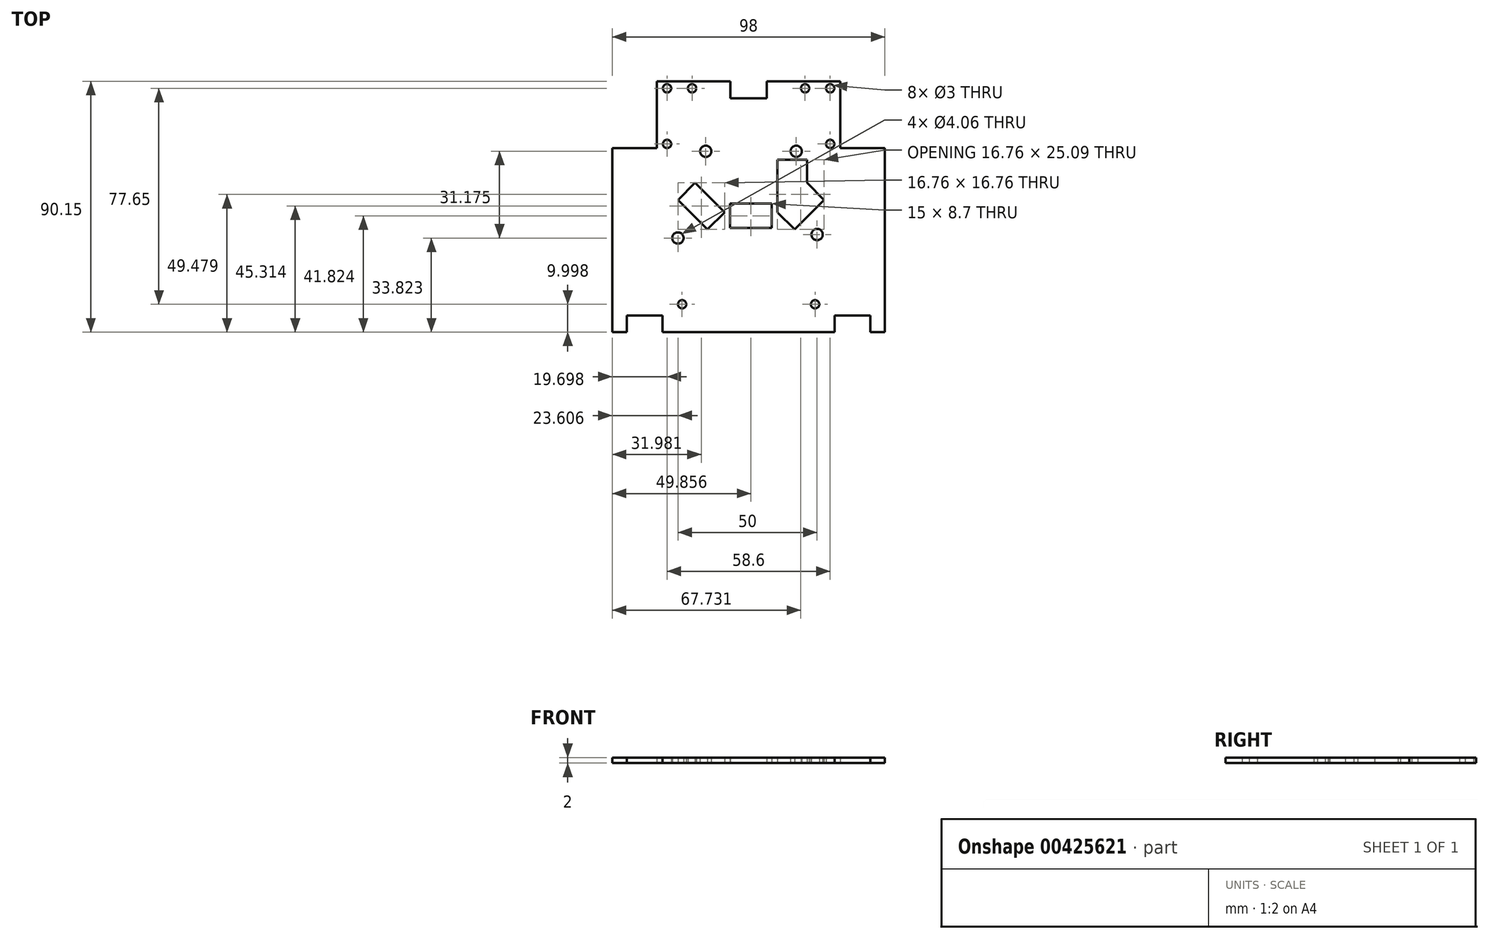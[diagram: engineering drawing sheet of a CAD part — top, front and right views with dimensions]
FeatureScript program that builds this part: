
annotation { "Feature Type Name" : "Feature", "Feature Type Description" : "" }
export const myFeature = defineFeature(function(context is Context, id is Id, definition is map)
    precondition{}
    {
        {
            var Q0;
            Q0=qCreatedBy(makeId("Top.planeOp"),FACE);
            var sketch = newSketch(context, id + "F0", { "sketchPlane" : qUnion([Q0])});
            skCircle(sketch, "E0", {"center": v(21.8, -32.76) * mm, "radius": 1.5 * mm});
            skCircle(sketch, "E1", {"center": v(18.2, 44.89) * mm, "radius": 1.5 * mm});
            skCircle(sketch, "E2", {"center": v(27.2, 24.89) * mm, "radius": 1.5 * mm});
            skCircle(sketch, "E3", {"center": v(-31.4, 44.89) * mm, "radius": 1.5 * mm});
            skCircle(sketch, "E4", {"center": v(27.2, 44.89) * mm, "radius": 1.5 * mm});
            skCircle(sketch, "E5", {"center": v(-22.4, 44.89) * mm, "radius": 1.5 * mm});
            skCircle(sketch, "E6", {"center": v(-31.4, 24.89) * mm, "radius": 1.5 * mm});
            skLineSegment(sketch, "E7", {"start": v(46.9, -42.76) * mm, "end": v(41.62, -42.76) * mm});
            skLineSegment(sketch, "E8", {"start": v(-51.1, -42.76) * mm, "end": v(-51.1, 23.39) * mm});
            skLineSegment(sketch, "E9", {"start": v(-35.1, 23.39) * mm, "end": v(-35.1, 47.39) * mm});
            skLineSegment(sketch, "E10", {"start": v(-35.1, 47.39) * mm, "end": v(-8.6, 47.39) * mm});
            skLineSegment(sketch, "E11", {"start": v(30.9, 47.39) * mm, "end": v(30.9, 23.39) * mm});
            skLineSegment(sketch, "E12", {"start": v(46.9, 23.39) * mm, "end": v(46.9, -42.76) * mm});
            skCircle(sketch, "E13", {"center": v(-27.5, -8.94) * mm, "radius": 2.03 * mm});
            skCircle(sketch, "E14", {"center": v(-17.5, 22.24) * mm, "radius": 2.03 * mm});
            skCircle(sketch, "E15", {"center": v(15, 22.24) * mm, "radius": 2.03 * mm});
            skCircle(sketch, "E16", {"center": v(22.5, -7.69) * mm, "radius": 2.03 * mm});
            skLineSegment(sketch, "E17", {"start": v(-8.74, 3.41) * mm, "end": v(6.26, 3.41) * mm});
            skLineSegment(sketch, "E18", {"start": v(-8.74, 3.41) * mm, "end": v(-8.74, -5.29) * mm});
            skLineSegment(sketch, "E19", {"start": v(-8.74, -5.29) * mm, "end": v(6.26, -5.29) * mm});
            skLineSegment(sketch, "E20", {"start": v(6.26, 3.41) * mm, "end": v(6.26, -5.29) * mm});
            skLineSegment(sketch, "E21", {"start": v(-10.74, 0.33) * mm, "end": v(-16.9, -5.83) * mm});
            skLineSegment(sketch, "E22", {"start": v(-10.74, 0.33) * mm, "end": v(-21.35, 10.93) * mm});
            skLineSegment(sketch, "E23", {"start": v(-21.35, 10.93) * mm, "end": v(-27.5, 4.78) * mm});
            skLineSegment(sketch, "E24", {"start": v(-16.9, -5.83) * mm, "end": v(-27.5, 4.78) * mm});
            skLineSegment(sketch, "E25", {"start": v(8.25, 0.33) * mm, "end": v(14.4, -5.83) * mm});
            skLineSegment(sketch, "E26", {"start": v(14.4, -5.83) * mm, "end": v(25.01, 4.78) * mm});
            skLineSegment(sketch, "E27", {"start": v(18.86, 10.93) * mm, "end": v(25.01, 4.78) * mm});
            skCircle(sketch, "E28", {"center": v(-26, -32.76) * mm, "radius": 1.5 * mm});
            skLineSegment(sketch, "E29", {"start": v(-35.1, 23.39) * mm, "end": v(-51.1, 23.39) * mm});
            skLineSegment(sketch, "E30", {"start": v(30.9, 23.39) * mm, "end": v(46.9, 23.39) * mm});
            skPoint(sketch, "E31", {"position": v(4.4, 47.32) * mm});
            skLineSegment(sketch, "E32.top", {"start": v(-8.6, 41.32) * mm, "end": v(4.4, 41.32) * mm});
            skLineSegment(sketch, "E32.left", {"start": v(-8.6, 47.39) * mm, "end": v(-8.6, 41.32) * mm});
            skLineSegment(sketch, "E32.right", {"start": v(4.4, 47.39) * mm, "end": v(4.4, 41.32) * mm});
            skLineSegment(sketch, "E33", {"start": v(8.25, 0.33) * mm, "end": v(8.25, 19.26) * mm});
            skLineSegment(sketch, "E34", {"start": v(8.25, 19.26) * mm, "end": v(18.86, 19.26) * mm});
            skLineSegment(sketch, "E35", {"start": v(18.86, 19.26) * mm, "end": v(18.86, 10.93) * mm});
            skLineSegment(sketch, "E36.bottom", {"start": v(-45.82, -36.76) * mm, "end": v(-33.02, -36.76) * mm});
            skLineSegment(sketch, "E36.left", {"start": v(-45.82, -36.76) * mm, "end": v(-45.82, -42.76) * mm});
            skLineSegment(sketch, "E36.right", {"start": v(-33.02, -36.76) * mm, "end": v(-33.02, -42.76) * mm});
            skLineSegment(sketch, "E37.bottom", {"start": v(28.82, -36.76) * mm, "end": v(41.62, -36.76) * mm});
            skLineSegment(sketch, "E37.left", {"start": v(28.82, -36.76) * mm, "end": v(28.82, -42.76) * mm});
            skLineSegment(sketch, "E37.right", {"start": v(41.62, -36.76) * mm, "end": v(41.62, -42.76) * mm});
            skLineSegment(sketch, "E38.trimOffspring", {"start": v(-45.82, -42.76) * mm, "end": v(-51.1, -42.76) * mm});
            skLineSegment(sketch, "E39.trimOffspring", {"start": v(28.82, -42.76) * mm, "end": v(-33.02, -42.76) * mm});
            skLineSegment(sketch, "E40.trimOffspring", {"start": v(4.4, 47.39) * mm, "end": v(30.9, 47.39) * mm});
            skSolve(sketch);
        }
        {
            var Q0;
            Q0=makeQuery(id+"F0.imprint","IMPRINT",FACE,{"disambiguationData":[TD([[makeQuery(id+"F0.imprint","IMPRINT",EDGE,{"derivedFrom":sQuery(id+"F0.wireOp",EDGE,"E0")}),-1.0]])]});
            extrude(context, id + "F1", {"entities" : qUnion([Q0]), "depth" : 2 * mm, "offsetDistance" : 25 * mm});
        }
    });
